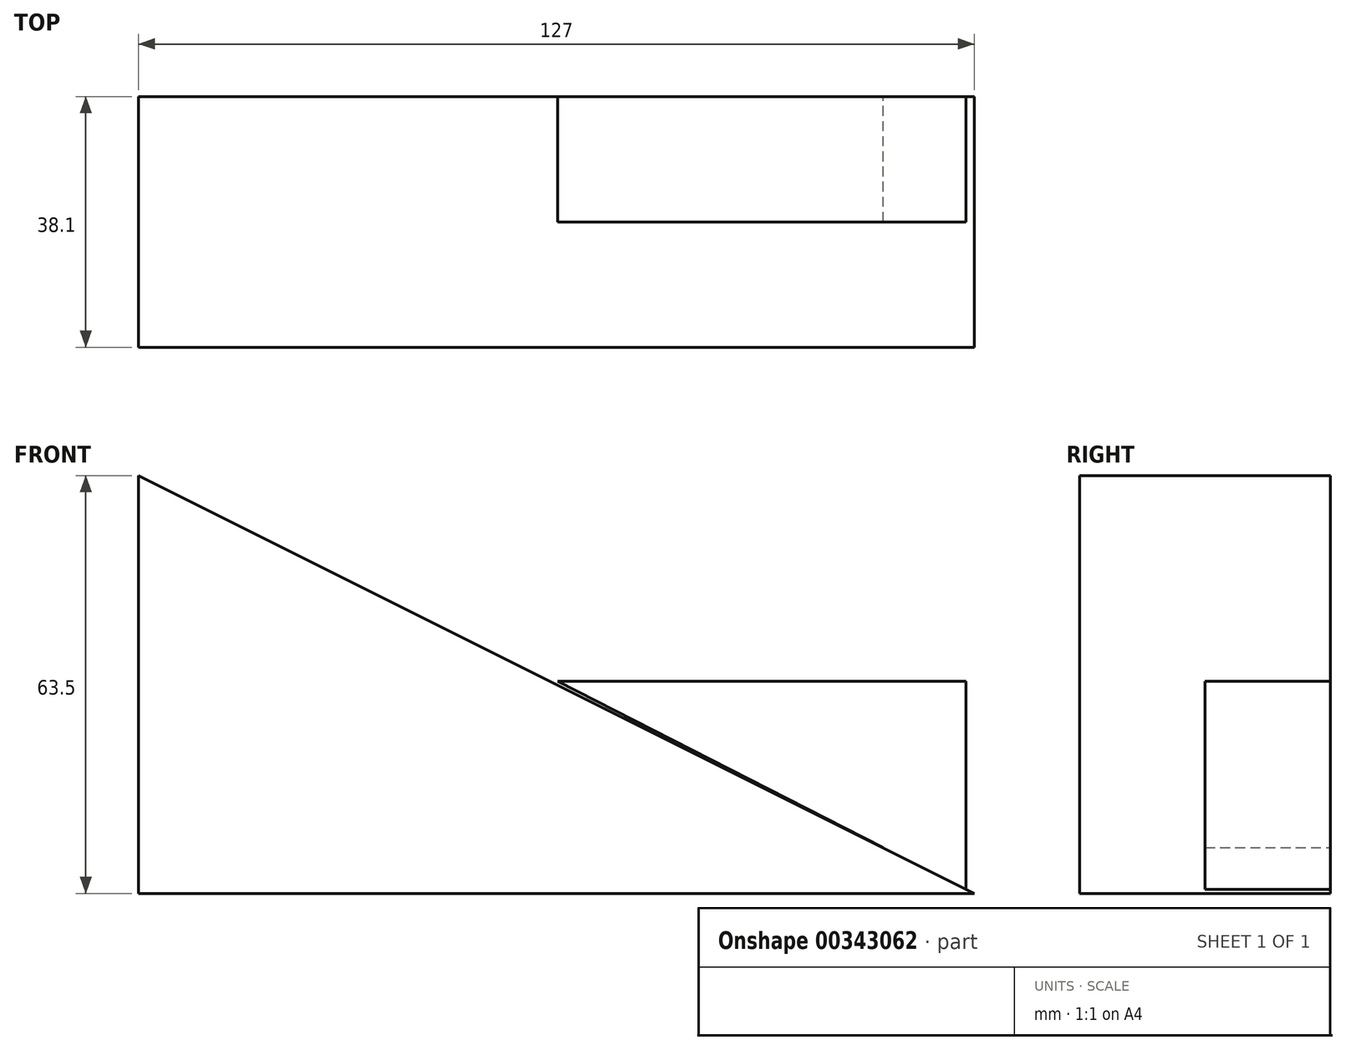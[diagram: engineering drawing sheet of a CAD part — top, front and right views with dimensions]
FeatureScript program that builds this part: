
annotation { "Feature Type Name" : "Feature", "Feature Type Description" : "" }
export const myFeature = defineFeature(function(context is Context, id is Id, definition is map)
    precondition{}
    {
        {
            var Q0;
            Q0=qCreatedBy(makeId("Front.planeOp"),FACE);
            var sketch = newSketch(context, id + "F0", { "sketchPlane" : qUnion([Q0])});
            skLineSegment(sketch, "E0", {"start": v(-52.3, -67.37) * mm, "end": v(74.7, -67.37) * mm});
            skLineSegment(sketch, "E1", {"start": v(-52.3, -67.37) * mm, "end": v(-52.3, -3.87) * mm});
            skPoint(sketch, "E2.start.orphan", {"position": v(-50.13, -3.87) * mm});
            skLineSegment(sketch, "E3", {"start": v(-52.3, -3.87) * mm, "end": v(74.7, -67.37) * mm});
            skSolve(sketch);
        }
        {
            var Q0;
            Q0 = qSketchRegion(id + "F0", true);
            extrude(context, id + "F1", {"entities" : qUnion([Q0]), "depth" : 38.1 * mm});
        }
        {
            var Q0;
            Q0=qCreatedBy(makeId("Front.planeOp"),FACE);
            var sketch = newSketch(context, id + "F2", { "sketchPlane" : qUnion([Q0])});
            skLineSegment(sketch, "E4", {"start": v(73.45, -66.9) * mm, "end": v(73.45, -35.14) * mm});
            skLineSegment(sketch, "E5", {"start": v(73.45, -35.14) * mm, "end": v(11.37, -35.14) * mm});
            skLineSegment(sketch, "E6", {"start": v(11.37, -35.14) * mm, "end": v(73.45, -66.9) * mm});
            skSolve(sketch);
        }
        {
            var Q0;
            Q0 = qSketchRegion(id + "F2", true);
            extrude(context, id + "F3", {"entities" : qUnion([Q0]), "operationType" : NewBodyOperationType.ADD, "depth" : 19.05 * mm});
        }
    });
